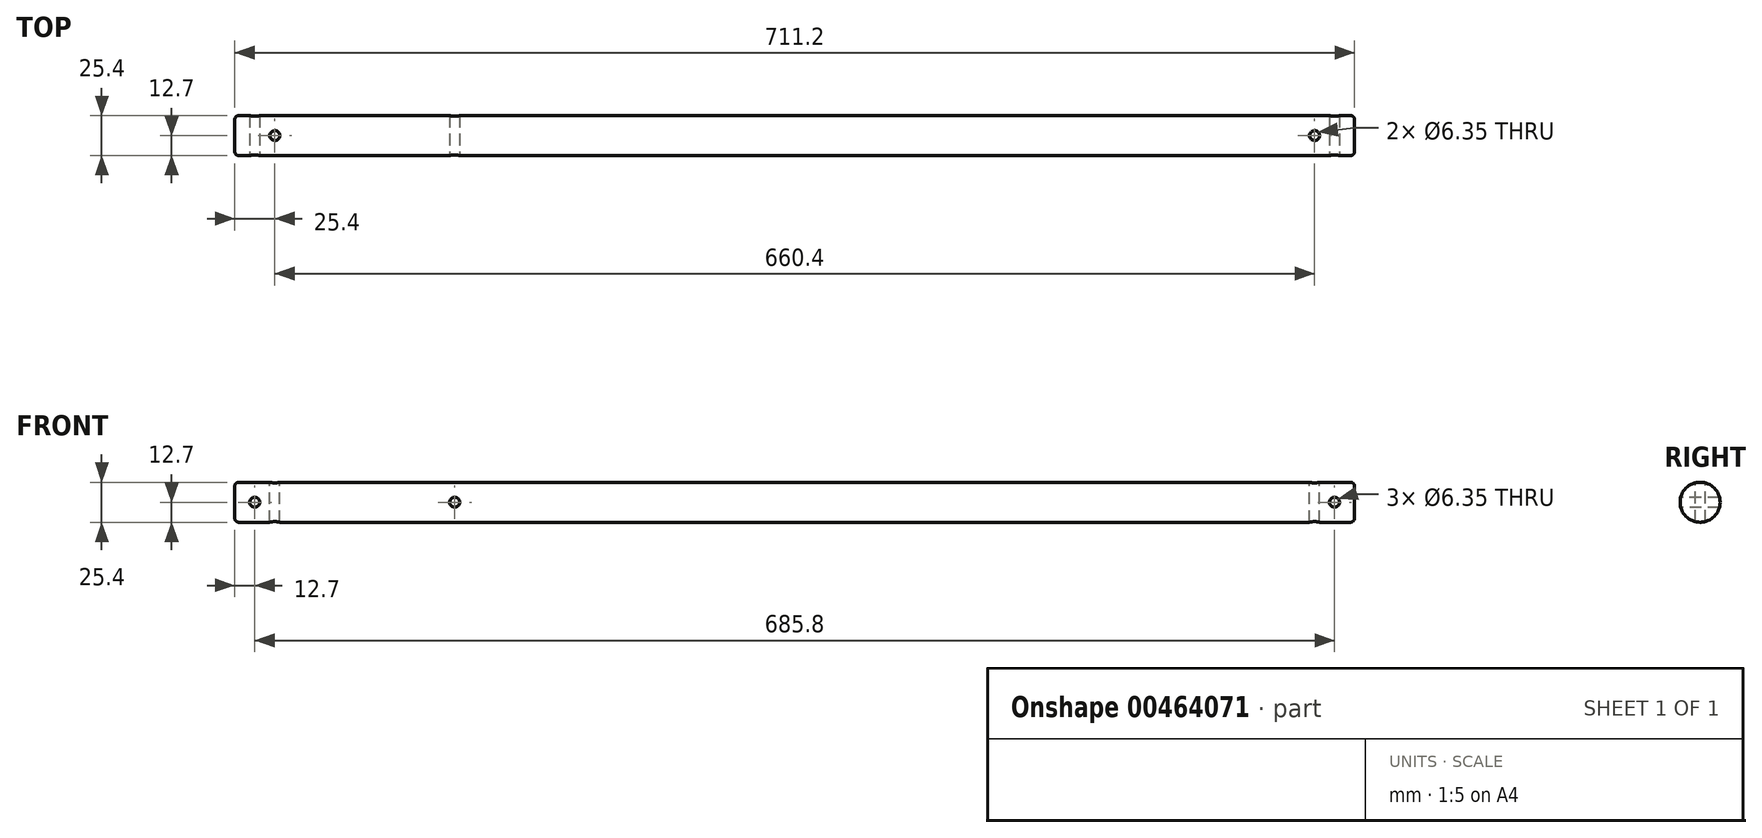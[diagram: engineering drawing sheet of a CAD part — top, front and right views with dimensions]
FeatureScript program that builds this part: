
annotation { "Feature Type Name" : "Feature", "Feature Type Description" : "" }
export const myFeature = defineFeature(function(context is Context, id is Id, definition is map)
    precondition{}
    {
        {
            var Q0;
            Q0=qCreatedBy(makeId("Right.planeOp"),FACE);
            var sketch = newSketch(context, id + "F0", { "sketchPlane" : qUnion([Q0])});
            skCircle(sketch, "E0", {"center": v(0, 0) * mm, "radius": 12.7 * mm});
            skSolve(sketch);
        }
        {
            var Q0;
            Q0=makeQuery(id+"F0.imprint","IMPRINT",FACE,{"disambiguationData":[TD([[makeQuery(id+"F0.imprint","IMPRINT",EDGE,{"derivedFrom":sQuery(id+"F0.wireOp",EDGE,"E0")}),1.0]])]});
            extrude(context, id + "F1", {"entities" : qUnion([Q0]), "depth" : 711.2 * mm});
        }
        {
            var Q0;
            Q0=qCreatedBy(makeId("Front.planeOp"),FACE);
            var sketch = newSketch(context, id + "F2", { "sketchPlane" : qUnion([Q0])});
            skLineSegment(sketch, "E1", {"start": v(0, 0) * mm, "end": v(12.7, 0) * mm});
            skCircle(sketch, "E2", {"center": v(12.7, 0) * mm, "radius": 3.18 * mm});
            skSolve(sketch);
        }
        {
            var Q0;
            Q0 = qSketchRegion(id + "F2", true);
            extrude(context, id + "F3", {"entities" : qUnion([Q0]), "operationType" : NewBodyOperationType.ADD, "depth" : 19.05 * mm});
        }
        {
            var Q0;
            Q0=makeQuery(id+"F1.opExtrude","CAP_EDGE",EDGE,{"disambiguationData":[OSD([sQuery(id+"F0.wireOp",EDGE,"E0")])],"isStart":true});
            var Q1;
            Q1=makeQuery(id+"F1.opExtrude","CAP_EDGE",EDGE,{"disambiguationData":[OSD([sQuery(id+"F0.wireOp",EDGE,"E0")])],"isStart":false});
            fillet(context, id + "F4", {"entities" : qUnion([Q0, Q1]), "radius" : 2.54 * mm, "tangentPropagation" : true, "allowEdgeOverflow" : false});
        }
        {
            var Q0;
            Q0=qCreatedBy(makeId("Front.planeOp"),FACE);
            cPlane(context, id + "F5", {"entities" : qUnion([Q0]), "cplaneType" : CPlaneType.OFFSET, "offset" : 6.35 * mm, "oppositeDirection" : true, "width" : 152.4 * mm, "height" : 152.4 * mm});
        }
        {
            var Q0;
            Q0=qCreatedBy(id+"F5.planeOp",FACE);
            var sketch = newSketch(context, id + "F6", { "sketchPlane" : qUnion([Q0])});
            skLineSegment(sketch, "E3", {"start": v(0, 0) * mm, "end": v(12.7, 0) * mm});
            skCircle(sketch, "E4", {"center": v(12.7, 0) * mm, "radius": 3.18 * mm});
            skLineSegment(sketch, "E5", {"start": v(12.7, 0) * mm, "end": v(698.5, 0) * mm});
            skCircle(sketch, "E6", {"center": v(698.5, 0) * mm, "radius": 3.18 * mm});
            skSolve(sketch);
        }
        {
            var Q0;
            Q0 = qSketchRegion(id + "F6", true);
            extrude(context, id + "F7", {"entities" : qUnion([Q0]), "operationType" : NewBodyOperationType.REMOVE, "oppositeDirection" : true, "depth" : 45.72 * mm, "hasSecondDirection" : true, "secondDirectionOppositeDirection" : false, "secondDirectionDepth" : 25.4 * mm});
        }
        {
            var Q0;
            Q0=qCreatedBy(makeId("Front.planeOp"),FACE);
            var sketch = newSketch(context, id + "F8", { "sketchPlane" : qUnion([Q0])});
            skLineSegment(sketch, "E7", {"start": v(0, 0) * mm, "end": v(139.7, 0) * mm});
            skCircle(sketch, "E8", {"center": v(139.7, 0) * mm, "radius": 3.18 * mm});
            skSolve(sketch);
        }
        {
            var Q0;
            Q0 = qSketchRegion(id + "F8", true);
            extrude(context, id + "F9", {"entities" : qUnion([Q0]), "operationType" : NewBodyOperationType.REMOVE, "oppositeDirection" : true, "depth" : 25.4 * mm, "hasSecondDirection" : true, "secondDirectionOppositeDirection" : false, "secondDirectionDepth" : 25.4 * mm});
        }
        {
            var Q0;
            Q0=qCreatedBy(makeId("Top.planeOp"),FACE);
            var sketch = newSketch(context, id + "F10", { "sketchPlane" : qUnion([Q0])});
            skLineSegment(sketch, "E9", {"start": v(0, 0) * mm, "end": v(25.4, 0) * mm});
            skCircle(sketch, "E10", {"center": v(25.4, 0) * mm, "radius": 3.18 * mm});
            skCircle(sketch, "E11", {"center": v(685.8, 0) * mm, "radius": 3.18 * mm});
            skSolve(sketch);
        }
        {
            var Q0;
            Q0 = qSketchRegion(id + "F10", true);
            extrude(context, id + "F11", {"entities" : qUnion([Q0]), "operationType" : NewBodyOperationType.REMOVE, "oppositeDirection" : true, "depth" : 25.4 * mm, "offsetDistance" : 25.4 * mm, "hasSecondDirection" : true, "secondDirectionOppositeDirection" : false, "secondDirectionDepth" : 25.4 * mm});
        }
    });
